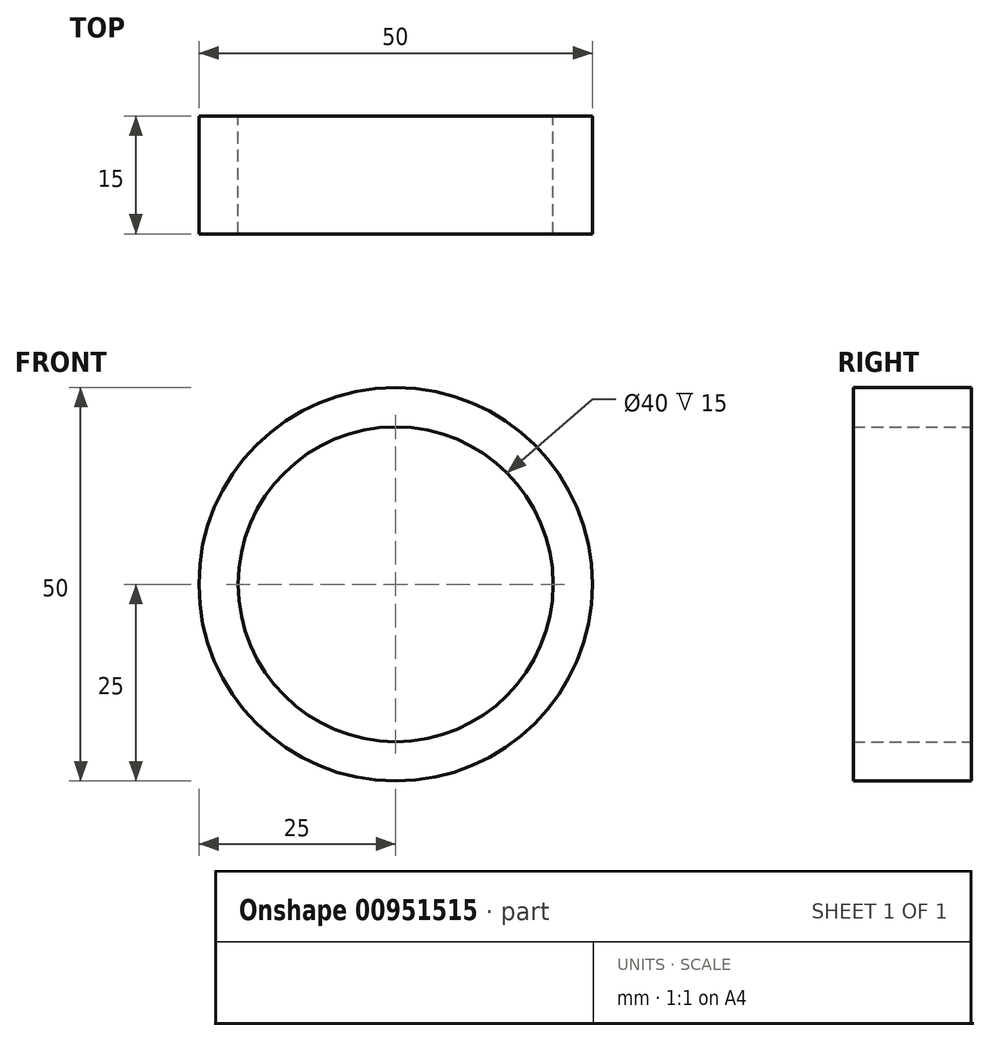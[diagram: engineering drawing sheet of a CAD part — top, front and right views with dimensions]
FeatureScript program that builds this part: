
annotation { "Feature Type Name" : "Feature", "Feature Type Description" : "" }
export const myFeature = defineFeature(function(context is Context, id is Id, definition is map)
    precondition{}
    {
        {
            var Q0;
            Q0=qCreatedBy(makeId("Front.planeOp"),FACE);
            var sketch = newSketch(context, id + "F0", { "sketchPlane" : qUnion([Q0])});
            skCircle(sketch, "E0", {"center": v(0, 0) * mm, "radius": 20 * mm});
            skCircle(sketch, "E1", {"center": v(0, 0) * mm, "radius": 25 * mm});
            skSolve(sketch);
        }
        {
            var Q0;
            Q0 = qSketchRegion(id + "F0", true);
            extrude(context, id + "F1", {"entities" : qUnion([Q0]), "depth" : 15 * mm, "offsetDistance" : 25 * mm});
        }
    });
